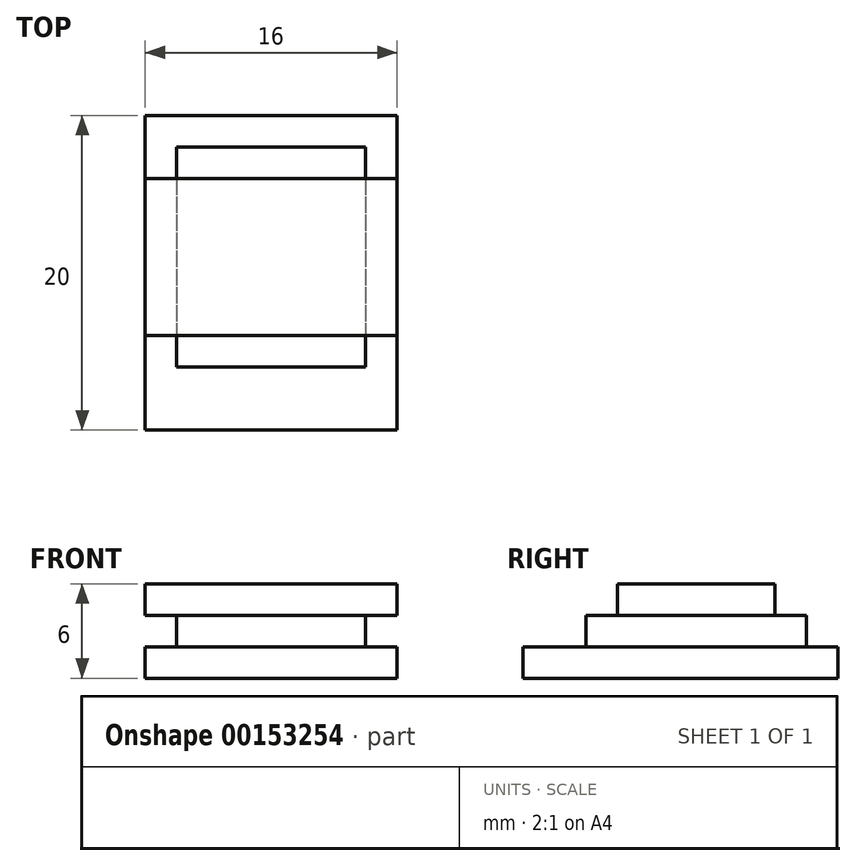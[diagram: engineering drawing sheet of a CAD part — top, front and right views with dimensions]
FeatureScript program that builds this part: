
annotation { "Feature Type Name" : "Feature", "Feature Type Description" : "" }
export const myFeature = defineFeature(function(context is Context, id is Id, definition is map)
    precondition{}
    {
        {
            assignVariable(context, id + "F0", {"name" : "T", "anyValue" : 2});
        }
        {
            var Q0;
            Q0=qCreatedBy(makeId("Top.planeOp"),FACE);
            var sketch = newSketch(context, id + "F1", { "sketchPlane" : qUnion([Q0])});
            skLineSegment(sketch, "E0.bottom", {"start": v(8, -10) * mm, "end": v(-8, -10) * mm});
            skLineSegment(sketch, "E0.top", {"start": v(8, 10) * mm, "end": v(-8, 10) * mm});
            skLineSegment(sketch, "E0.left", {"start": v(8, -10) * mm, "end": v(8, 10) * mm});
            skLineSegment(sketch, "E0.right", {"start": v(-8, -10) * mm, "end": v(-8, 10) * mm});
            skPoint(sketch, "E0.middle", {"position": v(0, 0) * mm});
            skSolve(sketch);
        }
        {
            var Q0;
            Q0=makeQuery(id+"F1.imprint","IMPRINT",FACE,{"disambiguationData":[TD([[makeQuery(id+"F1.imprint","IMPRINT",EDGE,{"derivedFrom":sQuery(id+"F1.wireOp",EDGE,"E0.bottom")}),-1.0]])]});
            extrude(context, id + "F2", {"entities" : qUnion([Q0]), "depth" : (getVariable(context, 'T')) * mm});
        }
        {
            var Q0;
            Q0=makeQuery(id+"F2.opExtrude","CAP_FACE",FACE,{"disambiguationData":[OSD([sQuery(id+"F1.wireOp",EDGE,"E0.bottom"),sQuery(id+"F1.wireOp",EDGE,"E0.top"),sQuery(id+"F1.wireOp",EDGE,"E0.left"),sQuery(id+"F1.wireOp",EDGE,"E0.right")])],"isStart":false});
            var sketch = newSketch(context, id + "F3", { "sketchPlane" : qUnion([Q0])});
            skLineSegment(sketch, "E1.bottom", {"start": v(-6, 8) * mm, "end": v(6, 8) * mm});
            skLineSegment(sketch, "E1.top", {"start": v(-6, -6) * mm, "end": v(6, -6) * mm});
            skLineSegment(sketch, "E1.left", {"start": v(-6, 8) * mm, "end": v(-6, -6) * mm});
            skLineSegment(sketch, "E1.right", {"start": v(6, 8) * mm, "end": v(6, -6) * mm});
            skSolve(sketch);
        }
        {
            var Q0;
            Q0=makeQuery(id+"F3.imprint","IMPRINT",FACE,{"disambiguationData":[TD([[makeQuery(id+"F3.imprint","IMPRINT",EDGE,{"derivedFrom":sQuery(id+"F3.wireOp",EDGE,"E1.bottom")}),-1.0]])]});
            extrude(context, id + "F4", {"entities" : qUnion([Q0]), "operationType" : NewBodyOperationType.ADD, "depth" : (getVariable(context, 'T')) * mm});
        }
        {
            var Q0;
            Q0=makeQuery(id+"F4.opExtrude","CAP_FACE",FACE,{"disambiguationData":[OSD([sQuery(id+"F3.wireOp",EDGE,"E1.bottom"),sQuery(id+"F3.wireOp",EDGE,"E1.top"),sQuery(id+"F3.wireOp",EDGE,"E1.left"),sQuery(id+"F3.wireOp",EDGE,"E1.right")])],"isStart":false});
            var sketch = newSketch(context, id + "F5", { "sketchPlane" : qUnion([Q0])});
            skLineSegment(sketch, "E2.bottom", {"start": v(-8, -4) * mm, "end": v(8, -4) * mm});
            skLineSegment(sketch, "E2.top", {"start": v(-8, 6) * mm, "end": v(8, 6) * mm});
            skLineSegment(sketch, "E2.left", {"start": v(-8, -4) * mm, "end": v(-8, 6) * mm});
            skLineSegment(sketch, "E2.right", {"start": v(8, -4) * mm, "end": v(8, 6) * mm});
            skSolve(sketch);
        }
        {
            var Q0;
            {var subQ0=sQuery(id+"F5.wireOp",EDGE,"E2.left");Q0=makeQuery(id+"F5.imprint","IMPRINT",FACE,{"disambiguationData":[TD([[makeQuery(id+"F5.imprint","IMPRINT",EDGE,{"derivedFrom":subQ0}),-1.0]])]});}
            var Q1;
            {var subQ0=sQuery(id+"F5.wireOp",EDGE,"E2.bottom");var subQ1=makeQuery(id+"F4.opExtrude","CAP_EDGE",EDGE,{"disambiguationData":[OSD([sQuery(id+"F3.wireOp",EDGE,"E1.left")])],"isStart":false});var subQ2=makeQuery(id+"F5.imprint","INTERSECT",VERTEX,{"derivedFrom":[subQ1,subQ0]});Q1=makeQuery(id+"F5.imprint","IMPRINT",FACE,{"disambiguationData":[TD([[makeQuery(id+"F5.imprint","IMPRINT",EDGE,{"disambiguationData":[TD([[subQ2,-1.0]])],"derivedFrom":subQ0}),1.0]])]});}
            var Q2;
            {var subQ0=sQuery(id+"F5.wireOp",EDGE,"E2.right");Q2=makeQuery(id+"F5.imprint","IMPRINT",FACE,{"disambiguationData":[TD([[makeQuery(id+"F5.imprint","IMPRINT",EDGE,{"derivedFrom":subQ0}),1.0]])]});}
            extrude(context, id + "F6", {"entities" : qUnion([Q0, Q1, Q2]), "operationType" : NewBodyOperationType.ADD, "depth" : (getVariable(context, 'T')) * mm});
        }
    });
